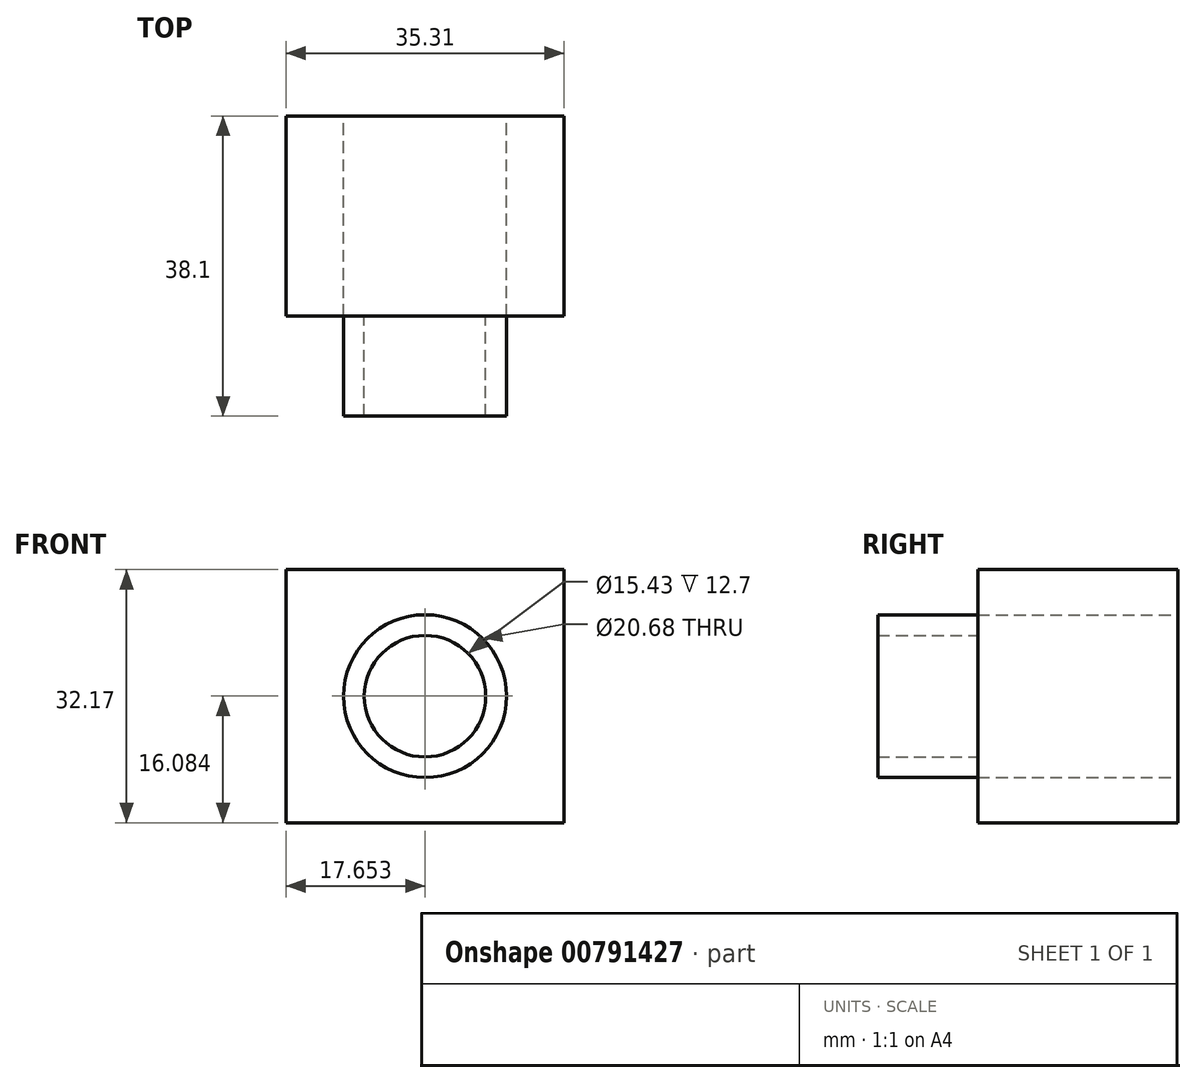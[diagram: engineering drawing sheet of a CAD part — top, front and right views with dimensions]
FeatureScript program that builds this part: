
annotation { "Feature Type Name" : "Feature", "Feature Type Description" : "" }
export const myFeature = defineFeature(function(context is Context, id is Id, definition is map)
    precondition{}
    {
        {
            var Q0;
            Q0=qCreatedBy(makeId("Front.planeOp"),FACE);
            var sketch = newSketch(context, id + "F0", { "sketchPlane" : qUnion([Q0])});
            skLineSegment(sketch, "E0", {"start": v(0, 0) * mm, "end": v(0, -32.17) * mm});
            skLineSegment(sketch, "E1", {"start": v(0, -32.17) * mm, "end": v(35.3, -32.17) * mm});
            skLineSegment(sketch, "E2", {"start": v(35.3, -32.17) * mm, "end": v(35.3, 0) * mm});
            skLineSegment(sketch, "E3", {"start": v(35.3, 0) * mm, "end": v(0, 0) * mm});
            skCircle(sketch, "E4", {"center": v(17.65, -16.09) * mm, "radius": 7.5 * mm});
            skPoint(sketch, "E4.centerSnap0", {"position": v(0, -16.09) * mm});
            skPoint(sketch, "E4.centerSnap1", {"position": v(17.65, 0) * mm});
            skCircle(sketch, "E5", {"center": v(17.65, -16.09) * mm, "radius": 10.34 * mm});
            skSolve(sketch);
        }
        {
            var Q0;
            Q0=makeQuery(id+"F0.imprint","IMPRINT",FACE,{"disambiguationData":[TD([[makeQuery(id+"F0.imprint","IMPRINT",EDGE,{"derivedFrom":sQuery(id+"F0.wireOp",EDGE,"E0")}),1.0]])]});
            extrude(context, id + "F1", {"entities" : qUnion([Q0]), "depth" : 25.4 * mm, "offsetDistance" : 25.4 * mm});
        }
        {
            var Q0;
            Q0=makeQuery(id+"F1.opExtrude","CAP_FACE",FACE,{"disambiguationData":[OSD([sQuery(id+"F0.wireOp",EDGE,"E0"),sQuery(id+"F0.wireOp",EDGE,"E1"),sQuery(id+"F0.wireOp",EDGE,"E2"),sQuery(id+"F0.wireOp",EDGE,"E3"),sQuery(id+"F0.wireOp",EDGE,"E5")])],"isStart":false});
            var sketch = newSketch(context, id + "F2", { "sketchPlane" : qUnion([Q0])});
            skCircle(sketch, "E6", {"center": v(17.65, -16.09) * mm, "radius": 7.72 * mm});
            skSolve(sketch);
        }
        {
            var Q0;
            Q0=makeQuery(id+"F2.imprint","IMPRINT",FACE,{"disambiguationData":[TD([[makeQuery(id+"F2.imprint","IMPRINT",EDGE,{"derivedFrom":sQuery(id+"F2.wireOp",EDGE,"E6")}),-1.0]])]});
            extrude(context, id + "F3", {"entities" : qUnion([Q0]), "depth" : 12.7 * mm, "offsetDistance" : 25.4 * mm});
        }
    });
